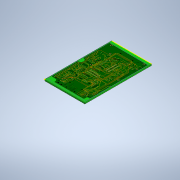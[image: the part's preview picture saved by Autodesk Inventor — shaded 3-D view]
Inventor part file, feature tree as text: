
AUTODESK INVENTOR PART (.ipt)
format: ipt  version: 2021 (Build 250183000, 183)  size: 414,208 bytes
history: native  units: in
note: dims shown in document units (in); Inventor stores cm internally (conversion verified against a paired STEP export)
features: sketch x2, extrude x1, other x1
ambient origin geometry x8: Origin, YZ Plane, XZ Plane, XY Plane, X Axis, Y Axis, Z Axis, Center Point
bodies: Solid1 (feature_tree)
feature tree (4):
  extrude  "Extrusion1"  Depth=0.061in
  sketch  "Sketch2"  dims[d2=2.9528in d3=0.0in]
  sketch  "Sketch1"  dims[d0=1.7717in d1=0.061in]
  other  "Image3"
